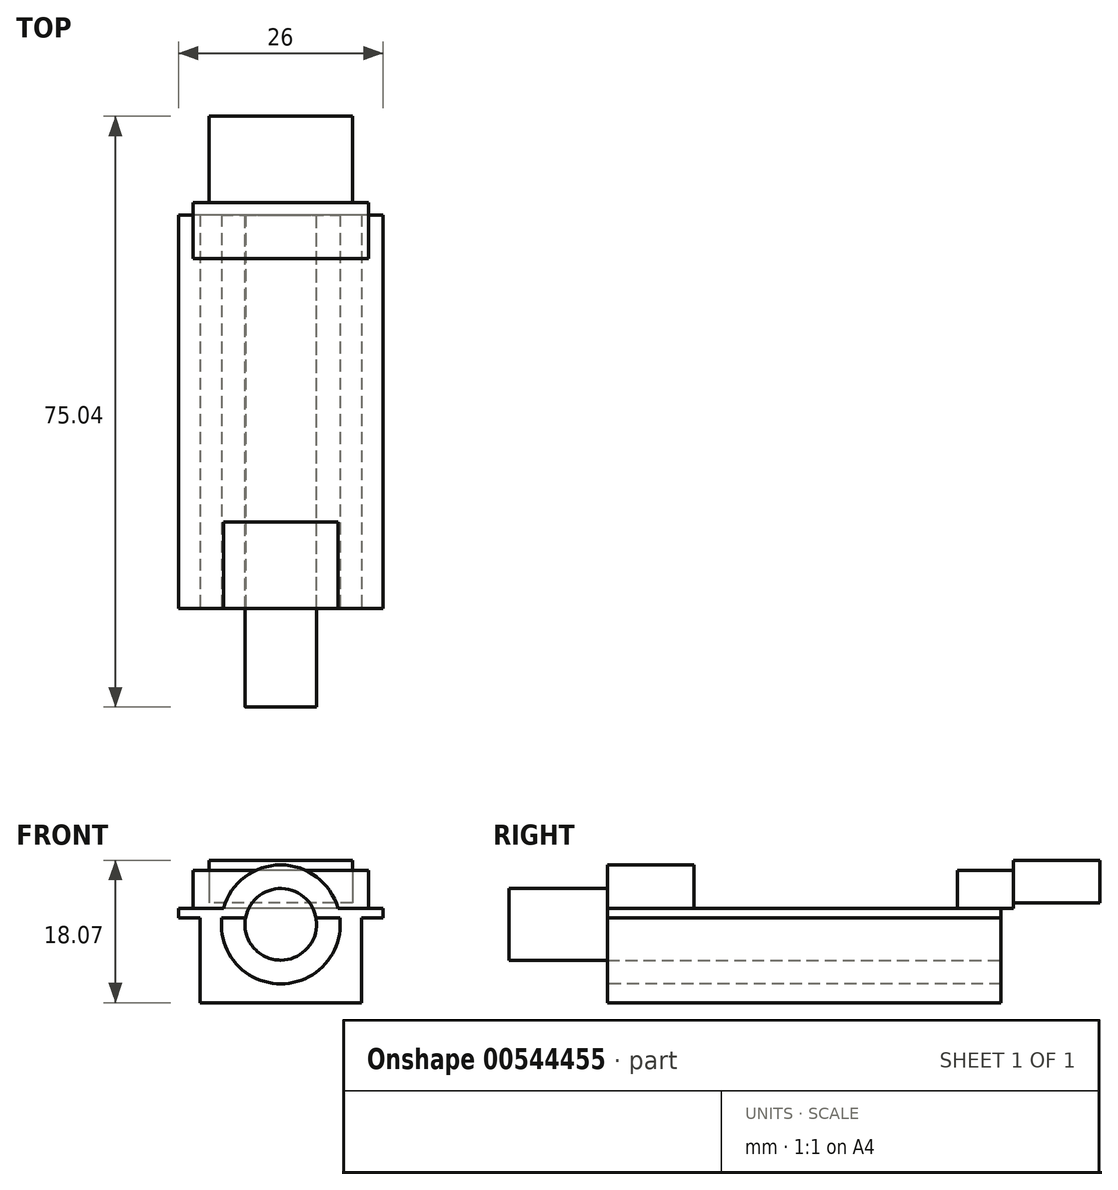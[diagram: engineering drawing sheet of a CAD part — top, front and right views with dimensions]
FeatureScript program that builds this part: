
annotation { "Feature Type Name" : "Feature", "Feature Type Description" : "" }
export const myFeature = defineFeature(function(context is Context, id is Id, definition is map)
    precondition{}
    {
        {
            assignVariable(context, id + "F0", {"name" : "pins", "anyValue" : 7});
        }
        {
            var Q0;
            Q0=qCreatedBy(makeId("Front.planeOp"),FACE);
            var sketch = newSketch(context, id + "F1", { "sketchPlane" : qUnion([Q0])});
            skLineSegment(sketch, "E0.top", {"start": v(10.25, -0.6) * mm, "end": v(-10.25, -0.6) * mm});
            skLineSegment(sketch, "E0.left", {"start": v(10.25, 10.2) * mm, "end": v(10.25, -0.6) * mm});
            skLineSegment(sketch, "E0.right", {"start": v(-10.25, 10.2) * mm, "end": v(-10.25, -0.6) * mm});
            skLineSegment(sketch, "E1.0", {"start": v(13, 11.4) * mm, "end": v(-13, 11.4) * mm});
            skLineSegment(sketch, "E2.0", {"start": v(13, 10.2) * mm, "end": v(-13, 10.2) * mm});
            skLineSegment(sketch, "E3", {"start": v(0, 16.2) * mm, "end": v(0, -5.38) * mm, "construction": true});
            skLineSegment(sketch, "E4.0", {"start": v(-13, 11.4) * mm, "end": v(-13, 10.2) * mm});
            skLineSegment(sketch, "E5", {"start": v(13, 11.4) * mm, "end": v(13, 10.2) * mm});
            skCircle(sketch, "E6", {"center": v(0, 9.35) * mm, "radius": 4.55 * mm});
            skCircle(sketch, "E7.0", {"center": v(0, 9.35) * mm, "radius": 7.55 * mm});
            skSolve(sketch);
        }
        {
            var Q0;
            {var subQ0=sQuery(id+"F1.wireOp",EDGE,"E6");var subQ1=sQuery(id+"F1.wireOp",EDGE,"E2.0");var subQ2=makeQuery(id+"F1.imprint","INTERSECT",VERTEX,{"disambiguationData":[OD(0.0)],"derivedFrom":[subQ1,subQ0]});Q0=makeQuery(id+"F1.imprint","IMPRINT",FACE,{"disambiguationData":[TD([[makeQuery(id+"F1.imprint","IMPRINT",EDGE,{"disambiguationData":[TD([[subQ2,-1.0]])],"derivedFrom":subQ1}),1.0]])]});}
            var Q1;
            {var subQ0=sQuery(id+"F1.wireOp",EDGE,"E6");var subQ1=sQuery(id+"F1.wireOp",EDGE,"E1.0");var subQ2=makeQuery(id+"F1.imprint","INTERSECT",VERTEX,{"disambiguationData":[OD(0.0)],"derivedFrom":[subQ1,subQ0]});Q1=makeQuery(id+"F1.imprint","IMPRINT",FACE,{"disambiguationData":[TD([[makeQuery(id+"F1.imprint","IMPRINT",EDGE,{"disambiguationData":[TD([[subQ2,-1.0]])],"derivedFrom":subQ1}),1.0]])]});}
            var Q2;
            {var subQ0=sQuery(id+"F1.wireOp",EDGE,"E6");var subQ1=sQuery(id+"F1.wireOp",EDGE,"E1.0");var subQ2=makeQuery(id+"F1.imprint","INTERSECT",VERTEX,{"disambiguationData":[OD(0.0)],"derivedFrom":[subQ1,subQ0]});Q2=makeQuery(id+"F1.imprint","IMPRINT",FACE,{"disambiguationData":[TD([[makeQuery(id+"F1.imprint","IMPRINT",EDGE,{"disambiguationData":[TD([[subQ2,-1.0]])],"derivedFrom":subQ1}),-1.0]])]});}
            extrude(context, id + "F2", {"entities" : qUnion([Q0, Q1, Q2]), "depth" : 12.5 * mm, "offsetDistance" : 25 * mm});
        }
        {
            var Q0;
            {var subQ0=sQuery(id+"F1.wireOp",EDGE,"E5");Q0=makeQuery(id+"F1.imprint","IMPRINT",FACE,{"disambiguationData":[TD([[makeQuery(id+"F1.imprint","IMPRINT",EDGE,{"derivedFrom":subQ0}),-1.0]])]});}
            var Q1;
            {var subQ0=sQuery(id+"F1.wireOp",EDGE,"E7.0");var subQ1=sQuery(id+"F1.wireOp",EDGE,"E1.0");var subQ2=makeQuery(id+"F1.imprint","INTERSECT",VERTEX,{"disambiguationData":[OD(0.0)],"derivedFrom":[subQ1,subQ0]});Q1=makeQuery(id+"F1.imprint","IMPRINT",FACE,{"disambiguationData":[TD([[makeQuery(id+"F1.imprint","IMPRINT",EDGE,{"disambiguationData":[TD([[subQ2,-1.0]])],"derivedFrom":subQ1}),1.0]])]});}
            var Q2;
            {var subQ0=sQuery(id+"F1.wireOp",EDGE,"E6");var subQ1=sQuery(id+"F1.wireOp",EDGE,"E1.0");var subQ2=makeQuery(id+"F1.imprint","INTERSECT",VERTEX,{"disambiguationData":[OD(0.0)],"derivedFrom":[subQ1,subQ0]});Q2=makeQuery(id+"F1.imprint","IMPRINT",FACE,{"disambiguationData":[TD([[makeQuery(id+"F1.imprint","IMPRINT",EDGE,{"disambiguationData":[TD([[subQ2,-1.0]])],"derivedFrom":subQ1}),1.0]])]});}
            var Q3;
            {var subQ0=sQuery(id+"F1.wireOp",EDGE,"E7.0");var subQ1=sQuery(id+"F1.wireOp",EDGE,"E1.0");var subQ2=makeQuery(id+"F1.imprint","INTERSECT",VERTEX,{"disambiguationData":[OD(1.0)],"derivedFrom":[subQ1,subQ0]});Q3=makeQuery(id+"F1.imprint","IMPRINT",FACE,{"disambiguationData":[TD([[makeQuery(id+"F1.imprint","IMPRINT",EDGE,{"disambiguationData":[TD([[subQ2,1.0]])],"derivedFrom":subQ1}),1.0]])]});}
            var Q4;
            {var subQ0=sQuery(id+"F1.wireOp",EDGE,"E4.0");Q4=makeQuery(id+"F1.imprint","IMPRINT",FACE,{"disambiguationData":[TD([[makeQuery(id+"F1.imprint","IMPRINT",EDGE,{"derivedFrom":subQ0}),1.0]])]});}
            var Q5;
            Q5=makeQuery(id+"F1.imprint","IMPRINT",FACE,{"disambiguationData":[TD([[makeQuery(id+"F1.imprint","IMPRINT",EDGE,{"derivedFrom":sQuery(id+"F1.wireOp",EDGE,"E0.top")}),-1.0]])]});
            var Q6;
            {var subQ0=sQuery(id+"F1.wireOp",EDGE,"E7.0");var subQ1=sQuery(id+"F1.wireOp",EDGE,"E2.0");var subQ2=makeQuery(id+"F1.imprint","INTERSECT",VERTEX,{"disambiguationData":[OD(0.0)],"derivedFrom":[subQ1,subQ0]});Q6=makeQuery(id+"F1.imprint","IMPRINT",FACE,{"disambiguationData":[TD([[makeQuery(id+"F1.imprint","IMPRINT",EDGE,{"disambiguationData":[TD([[subQ2,-1.0]])],"derivedFrom":subQ1}),1.0]])]});}
            var Q7;
            {var subQ0=sQuery(id+"F1.wireOp",EDGE,"E6");var subQ1=sQuery(id+"F1.wireOp",EDGE,"E2.0");var subQ2=makeQuery(id+"F1.imprint","INTERSECT",VERTEX,{"disambiguationData":[OD(0.0)],"derivedFrom":[subQ1,subQ0]});Q7=makeQuery(id+"F1.imprint","IMPRINT",FACE,{"disambiguationData":[TD([[makeQuery(id+"F1.imprint","IMPRINT",EDGE,{"disambiguationData":[TD([[subQ2,-1.0]])],"derivedFrom":subQ1}),1.0]])]});}
            extrude(context, id + "F3", {"entities" : qUnion([Q0, Q1, Q2, Q3, Q4, Q5, Q6, Q7]), "operationType" : NewBodyOperationType.ADD, "oppositeDirection" : true, "depth" : 50 * mm, "offsetDistance" : 25 * mm});
        }
        {
            var Q0;
            {var subQ0=sQuery(id+"F1.wireOp",EDGE,"E7.0");var subQ1=sQuery(id+"F1.wireOp",EDGE,"E1.0");var subQ2=makeQuery(id+"F1.imprint","INTERSECT",VERTEX,{"disambiguationData":[OD(0.0)],"derivedFrom":[subQ1,subQ0]});Q0=makeQuery(id+"F1.imprint","IMPRINT",FACE,{"disambiguationData":[TD([[makeQuery(id+"F1.imprint","IMPRINT",EDGE,{"disambiguationData":[TD([[subQ2,-1.0]])],"derivedFrom":subQ1}),-1.0]])]});}
            var Q1;
            {var subQ0=sQuery(id+"F1.wireOp",EDGE,"E6");var subQ1=sQuery(id+"F1.wireOp",EDGE,"E1.0");var subQ2=makeQuery(id+"F1.imprint","INTERSECT",VERTEX,{"disambiguationData":[OD(0.0)],"derivedFrom":[subQ1,subQ0]});Q1=makeQuery(id+"F1.imprint","IMPRINT",FACE,{"disambiguationData":[TD([[makeQuery(id+"F1.imprint","IMPRINT",EDGE,{"disambiguationData":[TD([[subQ2,-1.0]])],"derivedFrom":subQ1}),-1.0]])]});}
            extrude(context, id + "F4", {"entities" : qUnion([Q0, Q1]), "operationType" : NewBodyOperationType.ADD, "oppositeDirection" : true, "depth" : 11 * mm, "offsetDistance" : 25 * mm});
        }
        {
            var Q0;
            Q0=qCreatedBy(makeId("Right.planeOp"),FACE);
            var sketch = newSketch(context, id + "F5", { "sketchPlane" : qUnion([Q0])});
            skLineSegment(sketch, "E8.bottom", {"start": v(51.54, 17.47) * mm, "end": v(62.54, 17.47) * mm});
            skLineSegment(sketch, "E8.top", {"start": v(51.54, 12.07) * mm, "end": v(62.54, 12.07) * mm});
            skLineSegment(sketch, "E8.left", {"start": v(51.54, 17.47) * mm, "end": v(51.54, 12.07) * mm});
            skLineSegment(sketch, "E8.right", {"start": v(62.54, 17.47) * mm, "end": v(62.54, 12.07) * mm});
            skLineSegment(sketch, "E9.bottom", {"start": v(44.44, 16.2) * mm, "end": v(51.54, 16.2) * mm});
            skLineSegment(sketch, "E9.top", {"start": v(44.44, 11.4) * mm, "end": v(51.54, 11.4) * mm});
            skLineSegment(sketch, "E9.left", {"start": v(44.44, 16.2) * mm, "end": v(44.44, 11.4) * mm});
            skLineSegment(sketch, "E9.right", {"start": v(51.54, 16.2) * mm, "end": v(51.54, 11.4) * mm});
            skLineSegment(sketch, "E10", {"start": v(50, 11.4) * mm, "end": v(11, 11.4) * mm});
            skSolve(sketch);
        }
        {
            var Q0;
            {var subQ0=sQuery(id+"F5.wireOp",EDGE,"E8.bottom");Q0=makeQuery(id+"F5.imprint","IMPRINT",FACE,{"disambiguationData":[TD([[makeQuery(id+"F5.imprint","IMPRINT",EDGE,{"derivedFrom":subQ0}),-1.0]])]});}
            extrude(context, id + "F6", {"entities" : qUnion([Q0]), "depth" : (3 + 2.54 * (getVariable(context, 'pins') - 1)) * mm, "offsetDistance" : 25 * mm, "symmetric" : true});
        }
        {
            var Q0;
            {var subQ2=sQuery(id+"F5.wireOp",EDGE,"E9.bottom");Q0=makeQuery(id+"F5.imprint","IMPRINT",FACE,{"disambiguationData":[TD([[makeQuery(id+"F5.imprint","IMPRINT",EDGE,{"derivedFrom":subQ2}),-1.0]])]});}
            extrude(context, id + "F7", {"entities" : qUnion([Q0]), "depth" : (2.54 * (getVariable(context, 'pins') - 1) + 7.08) * mm, "offsetDistance" : 25 * mm, "symmetric" : true});
        }
    });
